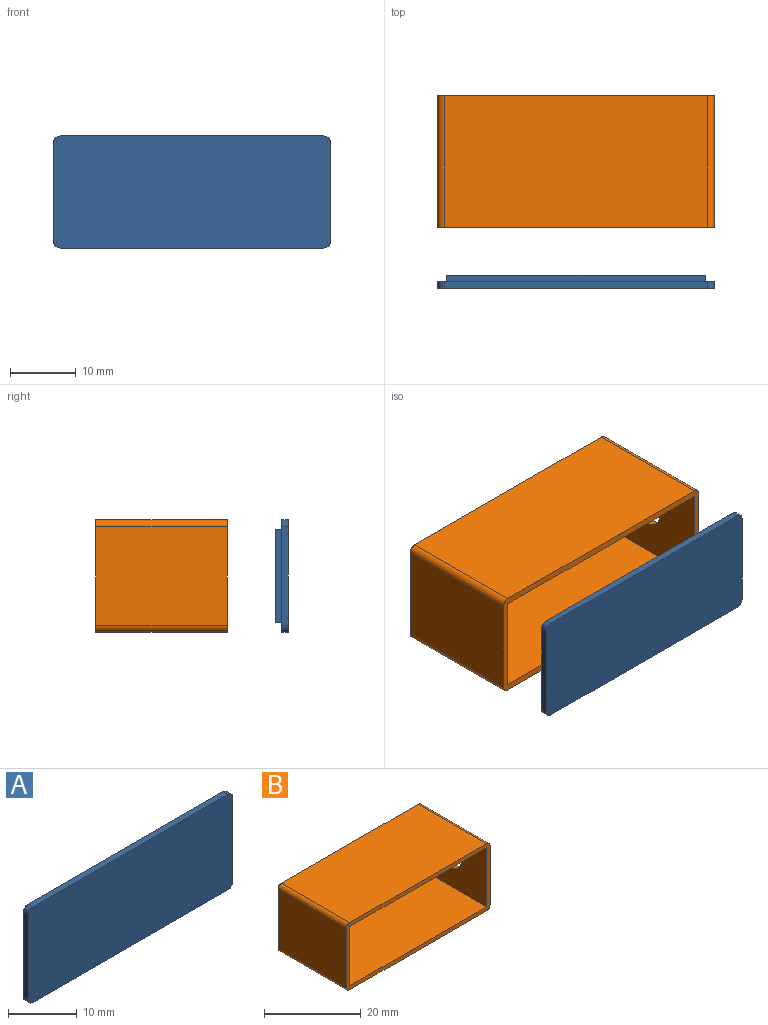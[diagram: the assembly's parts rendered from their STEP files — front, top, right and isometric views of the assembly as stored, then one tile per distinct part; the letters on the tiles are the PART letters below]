
ASSEMBLY  parts=2 mates=1
PART A: 15 faces, bbox 42x2x17 mm
  f0: cylinder r=1mm len=1mm, axis (0,1,0), area 1.6mm2, adj f1,f7,f8,f9
  f1: plane 40x1mm, normal (0,0,1), area 40mm2, adj f0,f2,f8,f9
  f2: cylinder r=1mm len=1mm, axis (0,1,0), area 1.6mm2, adj f1,f3,f8,f9
  f3: plane 15x1mm, normal (-1,0,0), area 15mm2, adj f2,f4,f8,f9
  f4: cylinder r=1mm len=1mm, axis (0,1,0), area 1.6mm2, adj f3,f5,f8,f9
  f5: plane 40x1mm, normal (0,0,-1), area 40mm2, adj f4,f6,f8,f9
  f6: cylinder r=1mm len=1mm, axis (0,1,0), area 1.6mm2, adj f5,f7,f8,f9
  f7: plane 15x1mm, normal (1,0,0), area 15mm2, adj f0,f6,f8,f9
  f8: plane 42x17mm, normal (0,-1,0), area 713.1mm2, adj f0,f1,f2,f3,f4,f5,f6,f7
  f9: plane 42x17mm, normal (0,1,0), area 156.5mm2, adj f0,f1,f2,f3,f4,f5,f6,f7
  f10: plane 14.2x1mm, normal (1,0,0), area 14.2mm2, adj f9,f11,f13,f14
  f11: plane 39.2x1mm, normal (0,0,1), area 39.2mm2, adj f9,f10,f12,f14
  f12: plane 14.2x1mm, normal (-1,0,0), area 14.2mm2, adj f9,f11,f13,f14
  f13: plane 39.2x1mm, normal (0,0,-1), area 39.2mm2, adj f9,f10,f12,f14
  f14: plane 39.2x14.2mm, normal (0,1,0), area 556.6mm2, adj f10,f11,f12,f13
PART B: 16 faces, bbox 42x20x17 mm
  f0: cylinder r=1mm len=20mm, axis (0,1,0), area 31.4mm2, adj f1,f11,f12,f13
  f1: plane 40x20mm, normal (0,0,1), area 800mm2, adj f0,f2,f12,f13
  f2: cylinder r=1mm len=20mm, axis (0,1,0), area 31.4mm2, adj f1,f3,f12,f13
  f3: plane 20x15mm, normal (-1,0,0), area 300mm2, adj f2,f4,f12,f13
  f4: cylinder r=1mm len=20mm, axis (0,1,0), area 31.4mm2, adj f3,f5,f12,f13
  f5: plane 40x20mm, normal (0,0,-1), area 800mm2, adj f4,f6,f12,f13
  f6: cylinder r=1mm len=20mm, axis (0,1,0), area 31.4mm2, adj f5,f11,f12,f13
  f7: plane 40x18mm, normal (0,0,-1), area 720mm2, adj f8,f10,f12,f14
  f8: plane 18x15mm, normal (-1,0,0), area 250.4mm2, adj f7,f9,f12,f14,f15
  f9: plane 40x18mm, normal (0,0,1), area 720mm2, adj f8,f10,f12,f14
  f10: plane 18x15mm, normal (1,0,0), area 270mm2, adj f7,f9,f12,f14
  f11: plane 20x15mm, normal (1,0,0), area 280.4mm2, adj f0,f6,f12,f13,f15
  f12: plane 42x17mm, normal (0,-1,0), area 113.1mm2, adj f0,f1,f2,f3,f4,f5,f6,f7
  f13: plane 42x17mm, normal (0,1,0), area 713.1mm2, adj f0,f1,f2,f3,f4,f5,f6,f11
  f14: plane 40x15mm, normal (0,-1,0), area 600mm2, adj f7,f8,f9,f10
  f15: cylinder r=2.5mm len=5mm, axis (1,0,0), area 15.7mm2, adj f8,f11
PLACE A t=(-3.41,12.57,22.62)mm
PLACE B t=(-3,40.81,22.9)mm
MATE slider A.f9 <-> B.f12  axis (0,1,0) through (-3,12.57,22.9)mm
